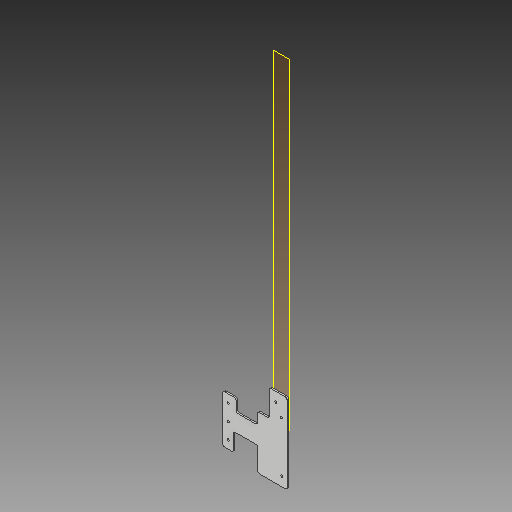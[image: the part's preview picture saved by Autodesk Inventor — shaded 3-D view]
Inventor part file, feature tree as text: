
AUTODESK INVENTOR PART (.ipt)
format: ipt  version: 2018 (Build 220112000, 112)  size: 150,528 bytes
history: native  units: mm
features: extrude x2, sketch x2, plane x1, fillet x1
ambient origin geometry x8: Origin, YZ Plane, XZ Plane, XY Plane, X Axis, Y Axis, Z Axis, Center Point
bodies: Solid1 (feature_tree)
feature tree (6):
  plane  "Work Plane1"
  extrude  "Extrusion1"  Depth=6.0mm TaperAngle=0.0deg
  fillet  "Fillet1"  Radius=92.0mm
  extrude  "Extrusion2"  Depth=40.0mm
  sketch  "Sketch1"  dims[d0=110.0mm d2=6.0mm d3=0.0mm d4=92.0mm]
  sketch  "Sketch2"  dims[d5=68.0mm d6=40.0mm d7=180.0mm d8=50.0mm d9=46.0mm d10=300.0mm d11=7.0mm d12=80.0mm d13=44.0mm d14=45.0mm d15=100.0mm d17=8.0mm d18=60.0mm d19=60.0mm d20=8.0mm d21=35.0mm d22=20.0mm d23=35.0mm d24=25.0mm d25=40.0mm d26=20.0mm d27=30.0mm d28=10.0mm d29=0.0mm]
